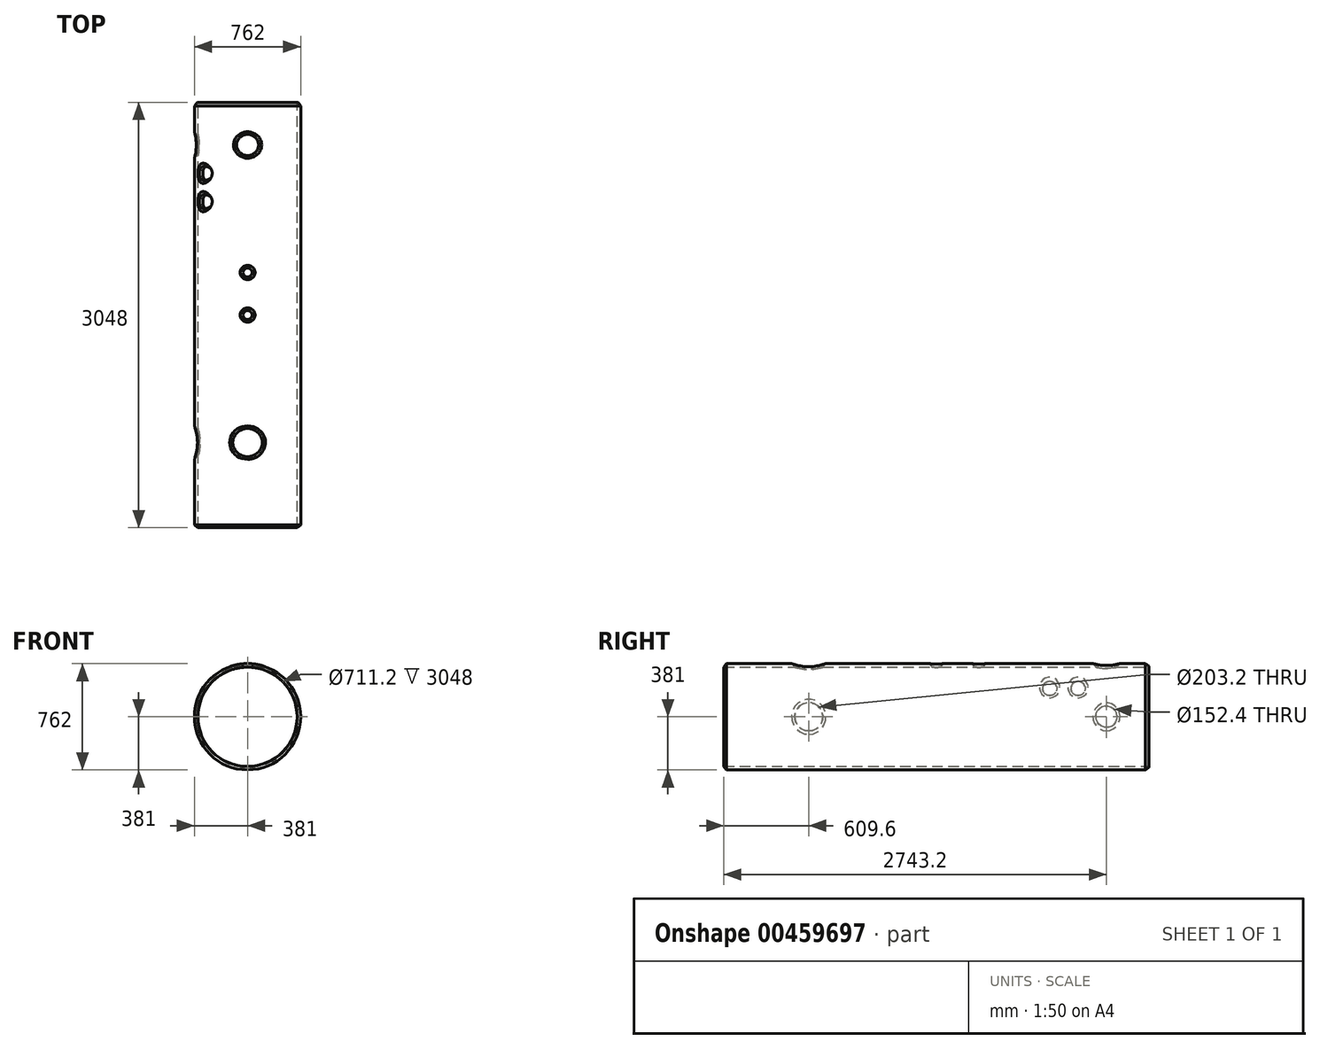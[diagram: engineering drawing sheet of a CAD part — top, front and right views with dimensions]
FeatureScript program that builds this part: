
annotation { "Feature Type Name" : "Feature", "Feature Type Description" : "" }
export const myFeature = defineFeature(function(context is Context, id is Id, definition is map)
    precondition{}
    {
        {
            var Q0;
            Q0=qCreatedBy(makeId("Front.planeOp"),FACE);
            var sketch = newSketch(context, id + "F0", { "sketchPlane" : qUnion([Q0])});
            skCircle(sketch, "E0", {"center": v(0, 0) * mm, "radius": 355.6 * mm});
            skCircle(sketch, "E1", {"center": v(0, 0) * mm, "radius": 381 * mm});
            skSolve(sketch);
        }
        {
            var Q0;
            Q0=makeQuery(id+"F0.imprint","IMPRINT",FACE,{"disambiguationData":[TD([[makeQuery(id+"F0.imprint","IMPRINT",EDGE,{"derivedFrom":sQuery(id+"F0.wireOp",EDGE,"E0")}),-1.0]])]});
            extrude(context, id + "F1", {"entities" : qUnion([Q0]), "depth" : 3048 * mm});
        }
        {
            var Q0;
            Q0=makeQuery(id+"F1.opExtrude","CAP_EDGE",EDGE,{"disambiguationData":[OSD([sQuery(id+"F0.wireOp",EDGE,"E1")])],"isStart":false});
            chamfer(context, id + "F2", {"entities" : qUnion([Q0]), "chamferType" : ChamferType.OFFSET_ANGLE, "width" : 24.13 * mm, "oppositeDirection" : false, "angle" : 37.5 * degree, "tangentPropagation" : true});
        }
        {
            var Q0;
            Q0=makeQuery(id+"F1.opExtrude","CAP_EDGE",EDGE,{"disambiguationData":[OSD([sQuery(id+"F0.wireOp",EDGE,"E1")])],"isStart":true});
            chamfer(context, id + "F3", {"entities" : qUnion([Q0]), "chamferType" : ChamferType.OFFSET_ANGLE, "width" : 24.13 * mm, "oppositeDirection" : false, "angle" : 37.5 * degree, "tangentPropagation" : true});
        }
        {
            var Q0;
            Q0=qCreatedBy(makeId("Top.planeOp"),FACE);
            var sketch = newSketch(context, id + "F4", { "sketchPlane" : qUnion([Q0])});
            skCircle(sketch, "E2", {"center": v(0, -1219.2) * mm, "radius": 31.75 * mm});
            skCircle(sketch, "E3", {"center": v(0, -304.8) * mm, "radius": 76.2 * mm});
            skCircle(sketch, "E4", {"center": v(0, -1524) * mm, "radius": 31.75 * mm});
            skCircle(sketch, "E5", {"center": v(0, -2438.4) * mm, "radius": 101.6 * mm});
            skSolve(sketch);
        }
        {
            var Q0;
            Q0 = qSketchRegion(id + "F4", true);
            extrude(context, id + "F5", {"entities" : qUnion([Q0]), "operationType" : NewBodyOperationType.REMOVE, "endBound" : BoundingType.THROUGH_ALL, "depth" : 25.4 * mm});
        }
        {
            var Q0;
            Q0=makeQuery(id+"F5.boolean.opBoolean","INTERSECT",EDGE,{"derivedFrom":[makeQuery(id+"F1.opExtrude","SWEPT_FACE",FACE,{"disambiguationData":[OSD([sQuery(id+"F0.wireOp",EDGE,"E1")])]}),makeQuery(id+"F5.opExtrude","SWEPT_FACE",FACE,{"disambiguationData":[OSD([sQuery(id+"F4.wireOp",EDGE,"E5")])]})]});
            var Q1;
            Q1=makeQuery(id+"F5.boolean.opBoolean","INTERSECT",EDGE,{"derivedFrom":[makeQuery(id+"F1.opExtrude","SWEPT_FACE",FACE,{"disambiguationData":[OSD([sQuery(id+"F0.wireOp",EDGE,"E1")])]}),makeQuery(id+"F5.opExtrude","SWEPT_FACE",FACE,{"disambiguationData":[OSD([sQuery(id+"F4.wireOp",EDGE,"E4")])]})]});
            var Q2;
            Q2=makeQuery(id+"F5.boolean.opBoolean","INTERSECT",EDGE,{"derivedFrom":[makeQuery(id+"F1.opExtrude","SWEPT_FACE",FACE,{"disambiguationData":[OSD([sQuery(id+"F0.wireOp",EDGE,"E1")])]}),makeQuery(id+"F5.opExtrude","SWEPT_FACE",FACE,{"disambiguationData":[OSD([sQuery(id+"F4.wireOp",EDGE,"E2")])]})]});
            var Q3;
            Q3=makeQuery(id+"F5.boolean.opBoolean","INTERSECT",EDGE,{"derivedFrom":[makeQuery(id+"F1.opExtrude","SWEPT_FACE",FACE,{"disambiguationData":[OSD([sQuery(id+"F0.wireOp",EDGE,"E1")])]}),makeQuery(id+"F5.opExtrude","SWEPT_FACE",FACE,{"disambiguationData":[OSD([sQuery(id+"F4.wireOp",EDGE,"E3")])]})]});
            chamfer(context, id + "F6", {"entities" : qUnion([Q0, Q1, Q2, Q3]), "chamferType" : ChamferType.OFFSET_ANGLE, "width" : 24.13 * mm, "oppositeDirection" : false, "angle" : 37.5 * degree, "tangentPropagation" : true});
        }
        {
            var Q0;
            Q0=qCreatedBy(makeId("Right.planeOp"),FACE);
            var sketch = newSketch(context, id + "F7", { "sketchPlane" : qUnion([Q0])});
            skCircle(sketch, "E6", {"center": v(-304.8, 0) * mm, "radius": 76.2 * mm});
            skCircle(sketch, "E7", {"center": v(-711.2, 203.2) * mm, "radius": 50.8 * mm});
            skCircle(sketch, "E8", {"center": v(-508, 203.2) * mm, "radius": 50.8 * mm});
            skCircle(sketch, "E9", {"center": v(-2438.4, 0) * mm, "radius": 101.6 * mm});
            skSolve(sketch);
        }
        {
            var Q0;
            Q0 = qSketchRegion(id + "F7", true);
            extrude(context, id + "F8", {"entities" : qUnion([Q0]), "operationType" : NewBodyOperationType.REMOVE, "endBound" : BoundingType.THROUGH_ALL, "oppositeDirection" : true, "depth" : 25.4 * mm});
        }
        {
            var Q0;
            Q0=makeQuery(id+"F8.boolean.opBoolean","INTERSECT",EDGE,{"derivedFrom":[makeQuery(id+"F1.opExtrude","SWEPT_FACE",FACE,{"disambiguationData":[OSD([sQuery(id+"F0.wireOp",EDGE,"E1")])]}),makeQuery(id+"F8.opExtrude","SWEPT_FACE",FACE,{"disambiguationData":[OSD([sQuery(id+"F7.wireOp",EDGE,"E6")])]})]});
            var Q1;
            Q1=makeQuery(id+"F8.boolean.opBoolean","INTERSECT",EDGE,{"derivedFrom":[makeQuery(id+"F1.opExtrude","SWEPT_FACE",FACE,{"disambiguationData":[OSD([sQuery(id+"F0.wireOp",EDGE,"E1")])]}),makeQuery(id+"F8.opExtrude","SWEPT_FACE",FACE,{"disambiguationData":[OSD([sQuery(id+"F7.wireOp",EDGE,"E8")])]})]});
            var Q2;
            Q2=makeQuery(id+"F8.boolean.opBoolean","INTERSECT",EDGE,{"derivedFrom":[makeQuery(id+"F1.opExtrude","SWEPT_FACE",FACE,{"disambiguationData":[OSD([sQuery(id+"F0.wireOp",EDGE,"E1")])]}),makeQuery(id+"F8.opExtrude","SWEPT_FACE",FACE,{"disambiguationData":[OSD([sQuery(id+"F7.wireOp",EDGE,"E7")])]})]});
            var Q3;
            Q3=makeQuery(id+"F8.boolean.opBoolean","INTERSECT",EDGE,{"derivedFrom":[makeQuery(id+"F1.opExtrude","SWEPT_FACE",FACE,{"disambiguationData":[OSD([sQuery(id+"F0.wireOp",EDGE,"E1")])]}),makeQuery(id+"F8.opExtrude","SWEPT_FACE",FACE,{"disambiguationData":[OSD([sQuery(id+"F7.wireOp",EDGE,"E9")])]})]});
            chamfer(context, id + "F9", {"entities" : qUnion([Q0, Q1, Q2, Q3]), "chamferType" : ChamferType.OFFSET_ANGLE, "width" : 24.13 * mm, "oppositeDirection" : false, "angle" : 37.5 * degree, "tangentPropagation" : true});
        }
    });
